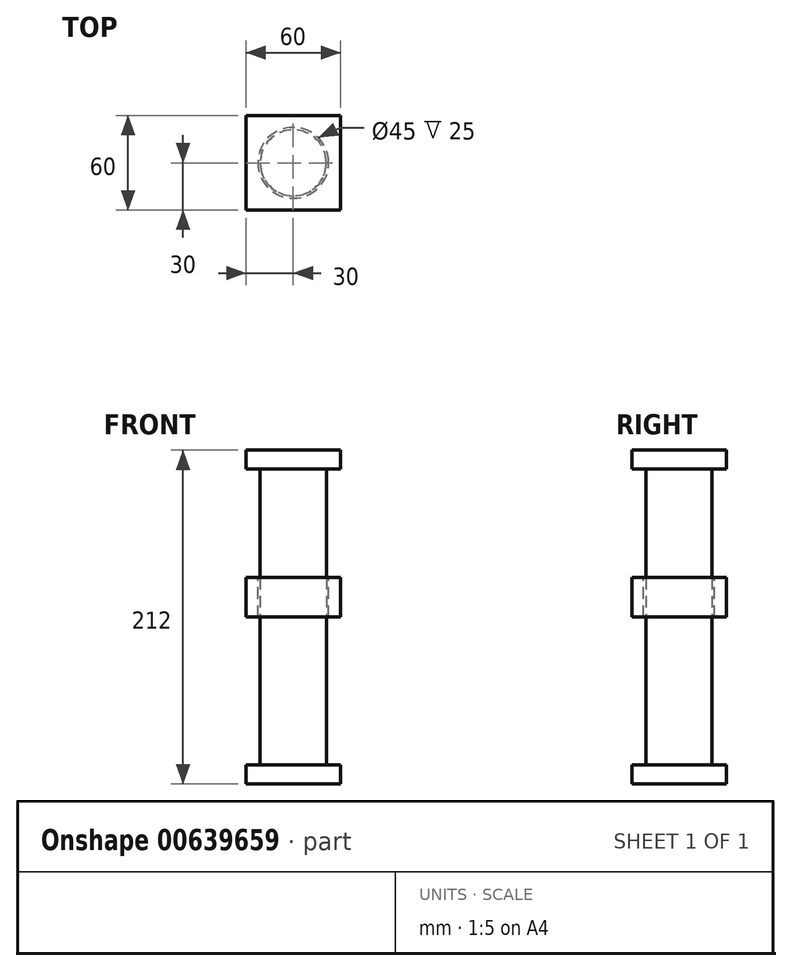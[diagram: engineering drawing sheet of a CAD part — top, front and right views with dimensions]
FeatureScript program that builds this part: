
annotation { "Feature Type Name" : "Feature", "Feature Type Description" : "" }
export const myFeature = defineFeature(function(context is Context, id is Id, definition is map)
    precondition{}
    {
        {
            var Q0;
            Q0=qCreatedBy(makeId("Top.planeOp"),FACE);
            var sketch = newSketch(context, id + "F0", { "sketchPlane" : qUnion([Q0])});
            skLineSegment(sketch, "E0.bottom", {"start": v(-30, -30) * mm, "end": v(30, -30) * mm});
            skLineSegment(sketch, "E0.top", {"start": v(-30, 30) * mm, "end": v(30, 30) * mm});
            skLineSegment(sketch, "E0.left", {"start": v(-30, -30) * mm, "end": v(-30, 30) * mm});
            skLineSegment(sketch, "E0.right", {"start": v(30, -30) * mm, "end": v(30, 30) * mm});
            skPoint(sketch, "E0.middle", {"position": v(0, 0) * mm});
            skSolve(sketch);
        }
        {
            var Q0;
            Q0=makeQuery(id+"F0.imprint","IMPRINT",FACE,{"disambiguationData":[TD([[makeQuery(id+"F0.imprint","IMPRINT",EDGE,{"derivedFrom":sQuery(id+"F0.wireOp",EDGE,"E0.bottom")}),1.0]])]});
            extrude(context, id + "F1", {"entities" : qUnion([Q0]), "depth" : 25 * mm, "offsetDistance" : 25 * mm});
        }
        {
            var Q0;
            Q0=makeQuery(id+"F1.opExtrude","CAP_FACE",FACE,{"disambiguationData":[OSD([sQuery(id+"F0.wireOp",EDGE,"E0.bottom"),sQuery(id+"F0.wireOp",EDGE,"E0.top"),sQuery(id+"F0.wireOp",EDGE,"E0.left"),sQuery(id+"F0.wireOp",EDGE,"E0.right")])],"isStart":false});
            var sketch = newSketch(context, id + "F2", { "sketchPlane" : qUnion([Q0])});
            skCircle(sketch, "E1", {"center": v(0, 0) * mm, "radius": 22.5 * mm});
            skSolve(sketch);
        }
        {
            var Q0;
            Q0=makeQuery(id+"F2.imprint","IMPRINT",FACE,{"disambiguationData":[TD([[makeQuery(id+"F2.imprint","IMPRINT",EDGE,{"derivedFrom":sQuery(id+"F2.wireOp",EDGE,"E1")}),1.0]])]});
            extrude(context, id + "F3", {"entities" : qUnion([Q0]), "operationType" : NewBodyOperationType.REMOVE, "oppositeDirection" : true, "depth" : 25 * mm, "offsetDistance" : 25 * mm});
        }
        {
            var Q0;
            Q0=qCreatedBy(makeId("Top.planeOp"),FACE);
            var sketch = newSketch(context, id + "F4", { "sketchPlane" : qUnion([Q0])});
            skCircle(sketch, "E2", {"center": v(0, 0) * mm, "radius": 21 * mm});
            skSolve(sketch);
        }
        {
            var Q0;
            Q0=makeQuery(id+"F4.imprint","IMPRINT",FACE,{"disambiguationData":[TD([[makeQuery(id+"F4.imprint","IMPRINT",EDGE,{"derivedFrom":sQuery(id+"F4.wireOp",EDGE,"E2")}),1.0]])]});
            extrude(context, id + "F5", {"entities" : qUnion([Q0]), "endBound" : BoundingType.SYMMETRIC, "depth" : 200 * mm, "offsetDistance" : 25 * mm});
        }
        {
            var Q0;
            Q0=makeQuery(id+"F5.opExtrude","CAP_FACE",FACE,{"disambiguationData":[OSD([sQuery(id+"F4.wireOp",EDGE,"E2")])],"isStart":false});
            var sketch = newSketch(context, id + "F6", { "sketchPlane" : qUnion([Q0])});
            skLineSegment(sketch, "E3.bottom", {"start": v(-30, -30) * mm, "end": v(30, -30) * mm});
            skLineSegment(sketch, "E3.top", {"start": v(-30, 30) * mm, "end": v(30, 30) * mm});
            skLineSegment(sketch, "E3.left", {"start": v(-30, -30) * mm, "end": v(-30, 30) * mm});
            skLineSegment(sketch, "E3.right", {"start": v(30, -30) * mm, "end": v(30, 30) * mm});
            skPoint(sketch, "E3.middle", {"position": v(0, 0) * mm});
            skSolve(sketch);
        }
        {
            var Q0;
            Q0=makeQuery(id+"F6.imprint","IMPRINT",FACE,{"disambiguationData":[TD([[makeQuery(id+"F6.imprint","IMPRINT",EDGE,{"derivedFrom":sQuery(id+"F6.wireOp",EDGE,"E3.bottom")}),1.0]])]});
            var Q1;
            Q1=makeQuery(id+"F6.imprint","IMPRINT",FACE,{"disambiguationData":[TD([[makeQuery(id+"F6.imprint","IMPRINT",EDGE,{"derivedFrom":makeQuery(id+"F5.opExtrude","CAP_EDGE",EDGE,{"disambiguationData":[OSD([sQuery(id+"F4.wireOp",EDGE,"E2")])],"isStart":false})}),1.0]])]});
            extrude(context, id + "F7", {"entities" : qUnion([Q0, Q1]), "operationType" : NewBodyOperationType.ADD, "endBound" : BoundingType.SYMMETRIC, "depth" : 12 * mm, "offsetDistance" : 25 * mm});
        }
        {
            var Q0;
            Q0=makeQuery(id+"F5.opExtrude","CAP_FACE",FACE,{"disambiguationData":[OSD([sQuery(id+"F4.wireOp",EDGE,"E2")])],"isStart":true});
            var sketch = newSketch(context, id + "F8", { "sketchPlane" : qUnion([Q0])});
            skLineSegment(sketch, "E4.bottom", {"start": v(30, -30) * mm, "end": v(-30, -30) * mm});
            skLineSegment(sketch, "E4.top", {"start": v(30, 30) * mm, "end": v(-30, 30) * mm});
            skLineSegment(sketch, "E4.left", {"start": v(30, -30) * mm, "end": v(30, 30) * mm});
            skLineSegment(sketch, "E4.right", {"start": v(-30, -30) * mm, "end": v(-30, 30) * mm});
            skPoint(sketch, "E4.middle", {"position": v(0, 0) * mm});
            skSolve(sketch);
        }
        {
            var Q0;
            Q0=makeQuery(id+"F8.imprint","IMPRINT",FACE,{"disambiguationData":[TD([[makeQuery(id+"F8.imprint","IMPRINT",EDGE,{"derivedFrom":sQuery(id+"F8.wireOp",EDGE,"E4.bottom")}),-1.0]])]});
            var Q1;
            Q1=makeQuery(id+"F8.imprint","IMPRINT",FACE,{"disambiguationData":[TD([[makeQuery(id+"F8.imprint","IMPRINT",EDGE,{"derivedFrom":makeQuery(id+"F5.opExtrude","CAP_EDGE",EDGE,{"disambiguationData":[OSD([sQuery(id+"F4.wireOp",EDGE,"E2")])],"isStart":true})}),-1.0]])]});
            extrude(context, id + "F9", {"entities" : qUnion([Q0, Q1]), "operationType" : NewBodyOperationType.ADD, "endBound" : BoundingType.SYMMETRIC, "depth" : 12 * mm, "offsetDistance" : 25 * mm});
        }
    });
